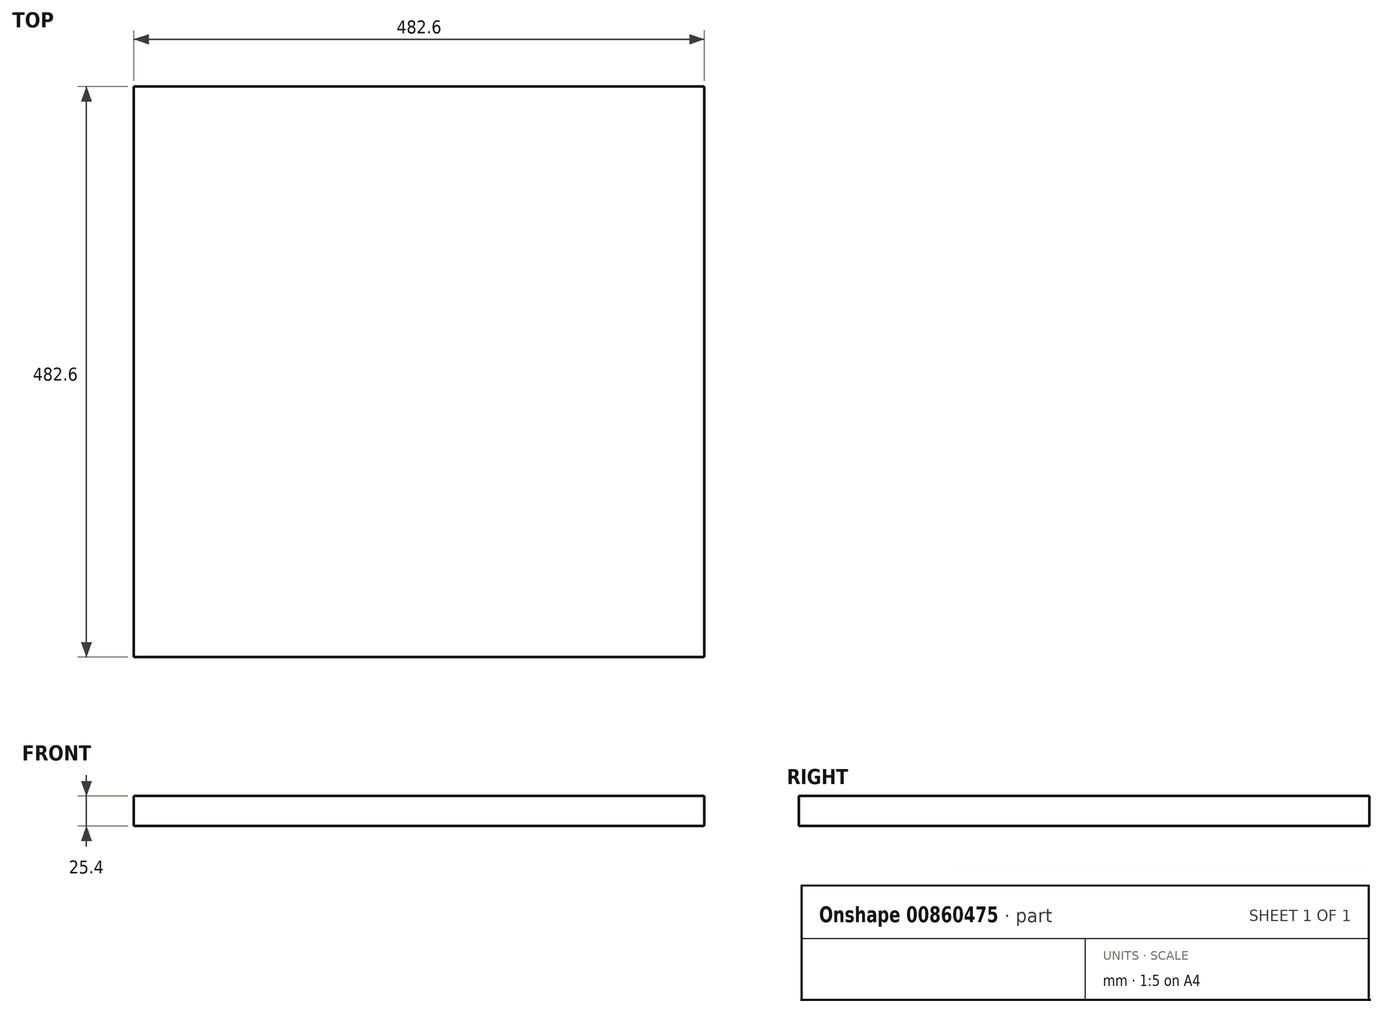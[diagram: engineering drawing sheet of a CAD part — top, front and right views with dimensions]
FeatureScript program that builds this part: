
annotation { "Feature Type Name" : "Feature", "Feature Type Description" : "" }
export const myFeature = defineFeature(function(context is Context, id is Id, definition is map)
    precondition{}
    {
        {
            var Q0;
            Q0=qCreatedBy(makeId("Top.planeOp"),FACE);
            var sketch = newSketch(context, id + "F0", { "sketchPlane" : qUnion([Q0])});
            skLineSegment(sketch, "E0.bottom", {"start": v(241.3, 241.3) * mm, "end": v(-241.3, 241.3) * mm});
            skLineSegment(sketch, "E0.top", {"start": v(241.3, -241.3) * mm, "end": v(-241.3, -241.3) * mm});
            skLineSegment(sketch, "E0.left", {"start": v(241.3, 241.3) * mm, "end": v(241.3, -241.3) * mm});
            skLineSegment(sketch, "E0.right", {"start": v(-241.3, 241.3) * mm, "end": v(-241.3, -241.3) * mm});
            skPoint(sketch, "E0.middle", {"position": v(0, 0) * mm});
            skSolve(sketch);
        }
        {
            var Q0;
            Q0 = qSketchRegion(id + "F0", true);
            extrude(context, id + "F1", {"entities" : qUnion([Q0]), "depth" : 25.4 * mm, "offsetDistance" : 25.4 * mm});
        }
    });
